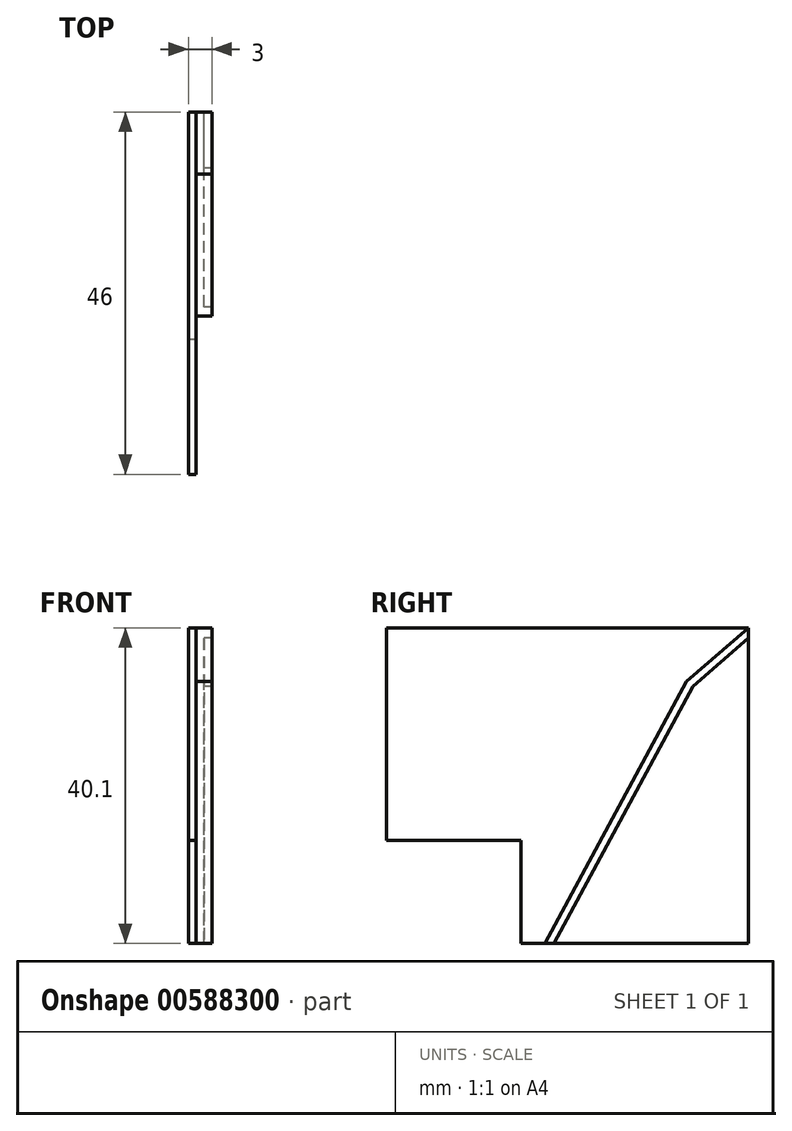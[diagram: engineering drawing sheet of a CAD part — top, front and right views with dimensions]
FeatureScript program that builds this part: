
annotation { "Feature Type Name" : "Feature", "Feature Type Description" : "" }
export const myFeature = defineFeature(function(context is Context, id is Id, definition is map)
    precondition{}
    {
        {
            var Q0;
            Q0=qCreatedBy(makeId("Right.planeOp"),FACE);
            var sketch = newSketch(context, id + "F0", { "sketchPlane" : qUnion([Q0])});
            skLineSegment(sketch, "E0.0", {"start": v(-35.16, 53.23) * mm, "end": v(-81.16, 53.23) * mm});
            skLineSegment(sketch, "E1.0", {"start": v(-35.16, 26.23) * mm, "end": v(-35.16, 53.23) * mm});
            skPoint(sketch, "E2.0", {"position": v(-40.16, 26.23) * mm});
            skLineSegment(sketch, "E3.0", {"start": v(-63.16, 26.23) * mm, "end": v(-62.35, 26.23) * mm});
            skLineSegment(sketch, "E4.0", {"start": v(-52.27, 26.23) * mm, "end": v(-52.27, 13.13) * mm});
            skLineSegment(sketch, "E5.0", {"start": v(-52.27, 13.13) * mm, "end": v(-81.16, 13.13) * mm});
            skLineSegment(sketch, "E6.0", {"start": v(-81.16, 53.23) * mm, "end": v(-81.16, 26.23) * mm});
            skLineSegment(sketch, "E7.0", {"start": v(-81.16, 26.23) * mm, "end": v(-81.16, 13.13) * mm});
            skLineSegment(sketch, "E8.0", {"start": v(-55.27, 13.13) * mm, "end": v(-73.27, 46.43) * mm});
            skLineSegment(sketch, "E9.0", {"start": v(-56.4, 13.13) * mm, "end": v(-74.06, 45.8) * mm});
            skLineSegment(sketch, "E10.0", {"start": v(-73.27, 46.43) * mm, "end": v(-81.16, 53.23) * mm});
            skLineSegment(sketch, "E11.0", {"start": v(-74.06, 45.8) * mm, "end": v(-81.16, 51.91) * mm});
            skLineSegment(sketch, "E12", {"start": v(-45.16, 26.23) * mm, "end": v(-35.16, 26.23) * mm});
            skLineSegment(sketch, "E13.trimOffspring", {"start": v(-52.27, 26.23) * mm, "end": v(-45.16, 26.23) * mm});
            skLineSegment(sketch, "E14.MirrorCS", {"start": v(-137.16, 53.23) * mm, "end": v(-91.16, 53.23) * mm});
            skLineSegment(sketch, "E15.MirrorCS", {"start": v(-91.16, 53.23) * mm, "end": v(-91.16, 26.23) * mm});
            skLineSegment(sketch, "E16.MirrorCS", {"start": v(-91.16, 26.23) * mm, "end": v(-91.16, 13.13) * mm});
            skLineSegment(sketch, "E17.MirrorCS", {"start": v(-120.06, 13.13) * mm, "end": v(-91.16, 13.13) * mm});
            skLineSegment(sketch, "E18.MirrorCS", {"start": v(-120.06, 26.23) * mm, "end": v(-120.06, 13.13) * mm});
            skLineSegment(sketch, "E19.MirrorCS", {"start": v(-120.06, 26.23) * mm, "end": v(-127.16, 26.23) * mm});
            skLineSegment(sketch, "E20.MirrorCS", {"start": v(-127.16, 26.23) * mm, "end": v(-137.16, 26.23) * mm});
            skLineSegment(sketch, "E21.MirrorCS", {"start": v(-137.16, 26.23) * mm, "end": v(-137.16, 53.23) * mm});
            skLineSegment(sketch, "E22.MirrorCS", {"start": v(-98.27, 45.8) * mm, "end": v(-91.16, 51.91) * mm});
            skLineSegment(sketch, "E23.MirrorCS", {"start": v(-99.06, 46.43) * mm, "end": v(-91.16, 53.23) * mm});
            skLineSegment(sketch, "E24.MirrorCS", {"start": v(-117.06, 13.13) * mm, "end": v(-99.06, 46.43) * mm});
            skLineSegment(sketch, "E25.MirrorCS", {"start": v(-115.92, 13.13) * mm, "end": v(-98.27, 45.8) * mm});
            skPoint(sketch, "E26.end.orphan", {"position": v(-86.16, 13.13) * mm});
            skSolve(sketch);
        }
        {
            var Q0;
            Q0=makeQuery(id+"F0.imprint","IMPRINT",FACE,{"disambiguationData":[TD([[makeQuery(id+"F0.imprint","IMPRINT",EDGE,{"derivedFrom":sQuery(id+"F0.wireOp",EDGE,"E14.MirrorCS")}),-1.0]])]});
            extrude(context, id + "F1", {"entities" : qUnion([Q0]), "depth" : 1 * mm, "offsetDistance" : 25 * mm});
        }
        {
            var Q0;
            {var subQ2=sQuery(id+"F0.wireOp",EDGE,"E22.MirrorCS");Q0=makeQuery(id+"F0.imprint","IMPRINT",FACE,{"disambiguationData":[TD([[makeQuery(id+"F0.imprint","IMPRINT",EDGE,{"derivedFrom":subQ2}),1.0]])]});}
            extrude(context, id + "F2", {"entities" : qUnion([Q0]), "operationType" : NewBodyOperationType.ADD, "depth" : 3 * mm, "offsetDistance" : 25 * mm});
        }
        {
            var Q0;
            {var subQ2=sQuery(id+"F0.wireOp",EDGE,"E16.MirrorCS");Q0=makeQuery(id+"F0.imprint","IMPRINT",FACE,{"disambiguationData":[TD([[makeQuery(id+"F0.imprint","IMPRINT",EDGE,{"derivedFrom":subQ2}),-1.0]])]});}
            extrude(context, id + "F3", {"entities" : qUnion([Q0]), "operationType" : NewBodyOperationType.ADD, "depth" : 2 * mm, "offsetDistance" : 25 * mm});
        }
    });
